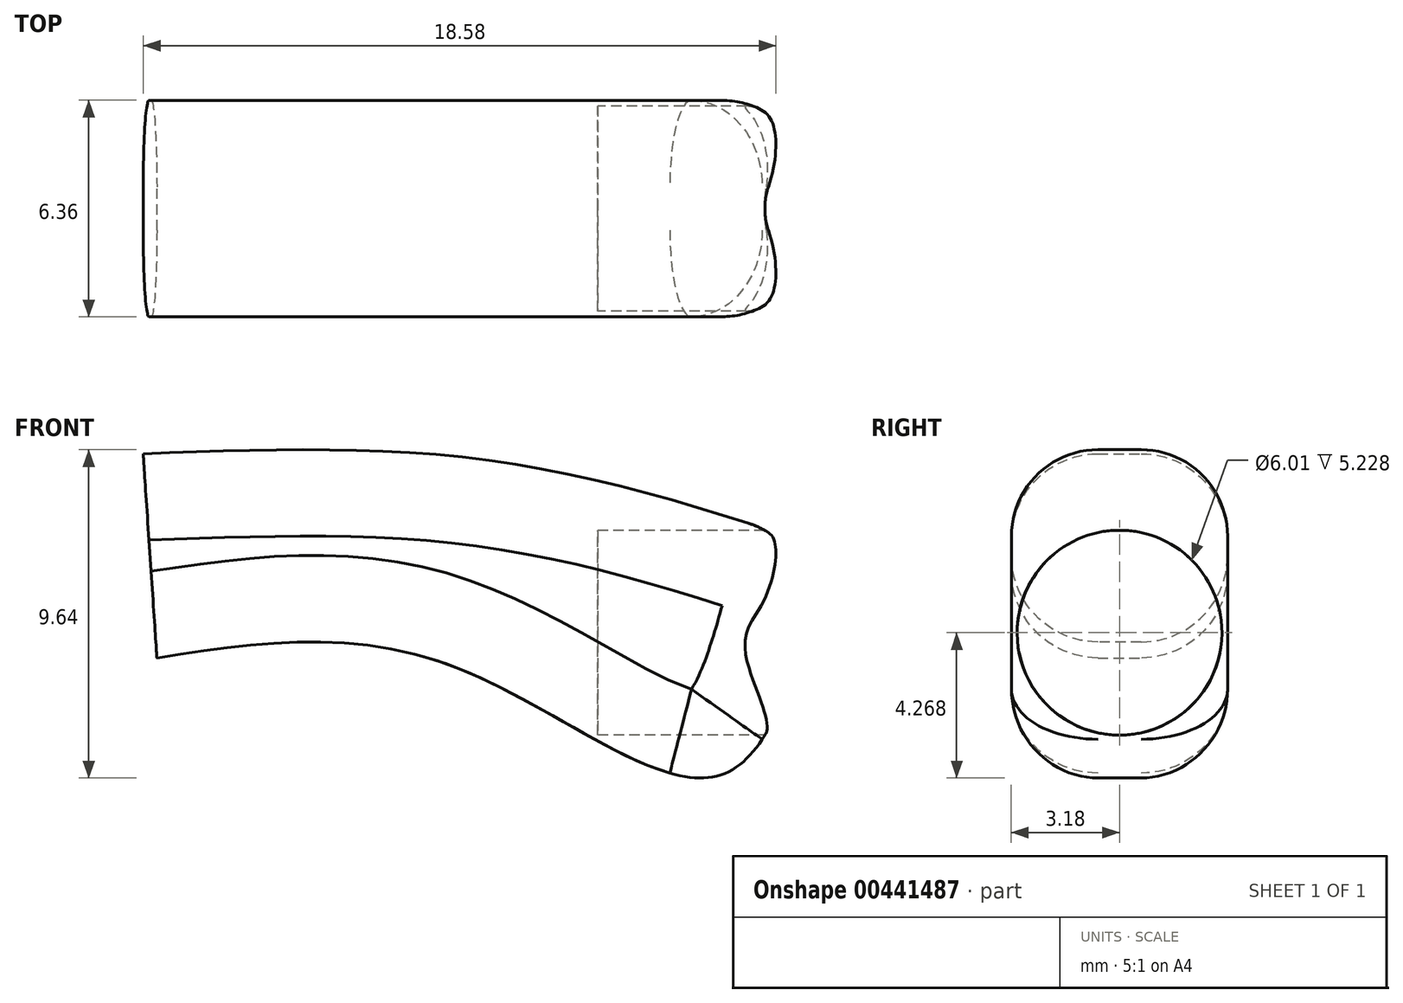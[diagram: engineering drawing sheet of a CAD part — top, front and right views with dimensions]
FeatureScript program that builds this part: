
annotation { "Feature Type Name" : "Feature", "Feature Type Description" : "" }
export const myFeature = defineFeature(function(context is Context, id is Id, definition is map)
    precondition{}
    {
        {
            var Q0;
            Q0=qCreatedBy(makeId("Front.planeOp"),FACE);
            var sketch = newSketch(context, id + "F0", { "sketchPlane" : qUnion([Q0])});
            skFitSpline(sketch, "E0", {"points": [v(-43.83, 38.28) * mm, v(-33.5, 38.07) * mm, v(-23.8, 35.51) * mm], "startDerivative": vector(20.76, 0.76) * mm, "endDerivative": vector(19.3, -6.32) * mm});
            skFitSpline(sketch, "E1", {"points": [v(-43.43, 32.29) * mm, v(-34.76, 32.05) * mm, v(-27, 28.82) * mm, v(-23.8, 35.51) * mm], "startDerivative": vector(24.94, 3.84) * mm, "endDerivative": vector(6.85, 29.57) * mm});
            skFitSpline(sketch, "E2", {"points": [v(-24.46, 34.17) * mm, v(-23.8, 35.51) * mm], "startDerivative": vector(0.65, 1.34) * mm, "endDerivative": vector(0.65, 1.34) * mm});
            skFitSpline(sketch, "E3", {"points": [v(-43.83, 38.28) * mm, v(-43.43, 32.29) * mm], "startDerivative": vector(0.4, -6) * mm, "endDerivative": vector(0.4, -6) * mm});
            skSolve(sketch);
        }
        {
            var Q0;
            Q0 = qSketchRegion(id + "F0", true);
            extrude(context, id + "F1", {"entities" : qUnion([Q0]), "endBound" : BoundingType.SYMMETRIC, "depth" : 6.35 * mm});
        }
        {
            var Q0;
            Q0=makeQuery(id+"F1.opExtrude","CAP_EDGE",EDGE,{"disambiguationData":[OSD([sQuery(id+"F0.wireOp",EDGE,"E0")])],"isStart":true});
            fillet(context, id + "F2", {"entities" : qUnion([Q0]), "radius" : 2.54 * mm, "tangentPropagation" : true, "allowEdgeOverflow" : false});
        }
        {
            var Q0;
            Q0=makeQuery(id+"F1.opExtrude","CAP_EDGE",EDGE,{"disambiguationData":[OSD([sQuery(id+"F0.wireOp",EDGE,"E0")])],"isStart":false});
            fillet(context, id + "F3", {"entities" : qUnion([Q0]), "radius" : 2.54 * mm, "tangentPropagation" : true, "allowEdgeOverflow" : false});
        }
        {
            var Q0;
            Q0=makeQuery(id+"F1.opExtrude","CAP_EDGE",EDGE,{"disambiguationData":[OSD([sQuery(id+"F0.wireOp",EDGE,"E1")])],"isStart":false});
            fillet(context, id + "F4", {"entities" : qUnion([Q0]), "radius" : 2.54 * mm, "tangentPropagation" : true, "allowEdgeOverflow" : false});
        }
        {
            var Q0;
            Q0=qCreatedBy(makeId("Right.planeOp"),FACE);
            var sketch = newSketch(context, id + "F5", { "sketchPlane" : qUnion([Q0])});
            skCircle(sketch, "E4", {"center": v(0, 33.03) * mm, "radius": 3 * mm});
            skSolve(sketch);
        }
        {
            var Q0;
            Q0=makeQuery(id+"F5.imprint","IMPRINT",FACE,{"disambiguationData":[TD([[makeQuery(id+"F5.imprint","IMPRINT",EDGE,{"derivedFrom":sQuery(id+"F5.wireOp",EDGE,"E4")}),1.0]])]});
            extrude(context, id + "F6", {"entities" : qUnion([Q0]), "operationType" : NewBodyOperationType.REMOVE, "endBound" : BoundingType.SYMMETRIC, "depth" : 60.96 * mm});
        }
    });
